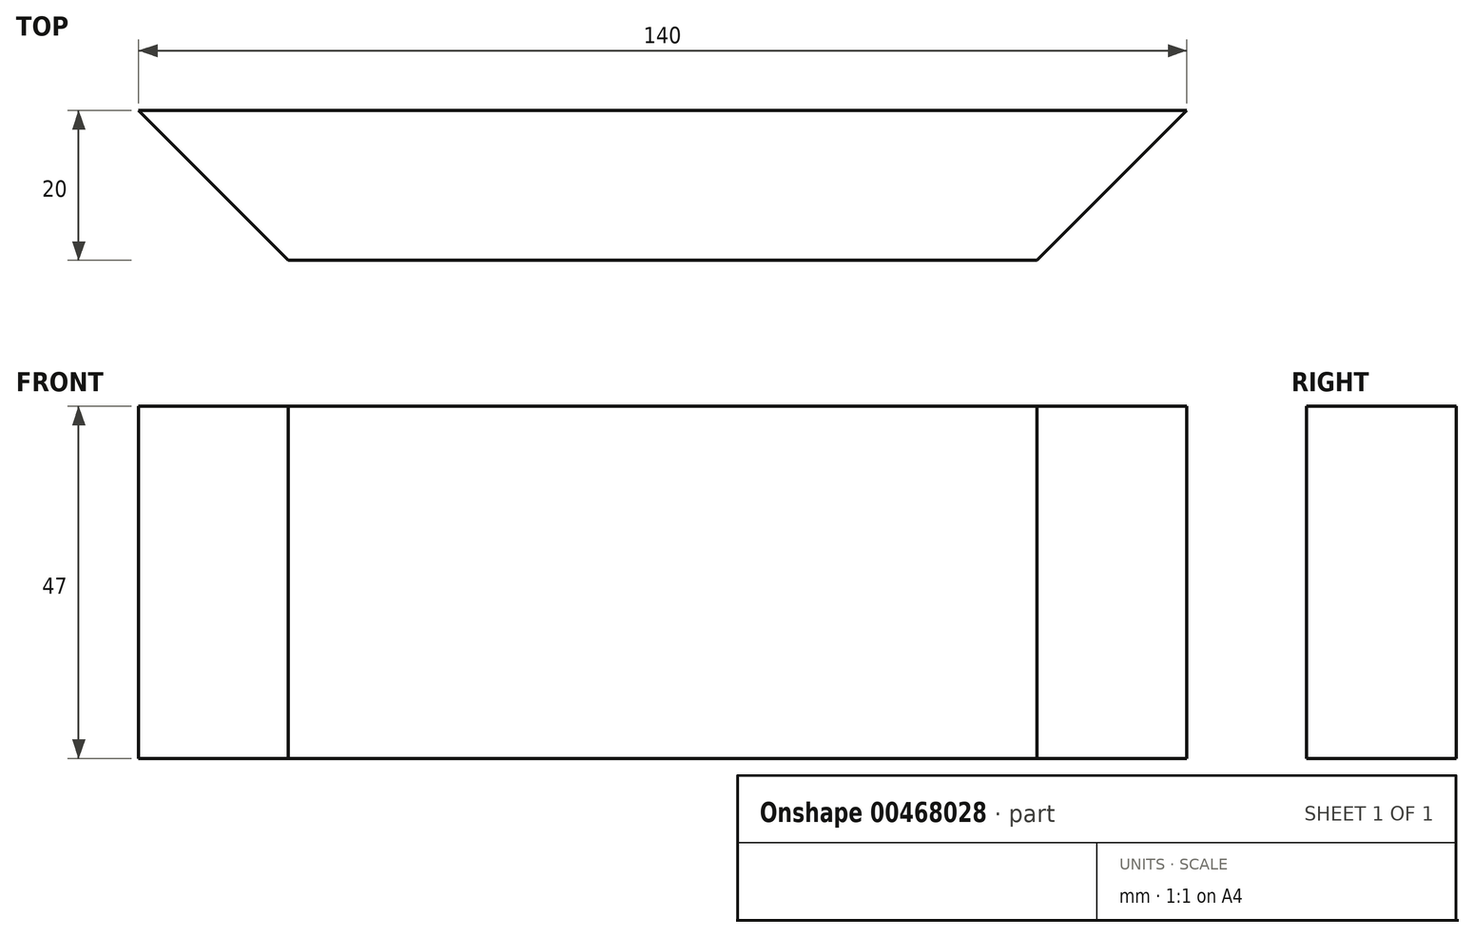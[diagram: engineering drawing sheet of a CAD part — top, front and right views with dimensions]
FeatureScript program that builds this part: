
annotation { "Feature Type Name" : "Feature", "Feature Type Description" : "" }
export const myFeature = defineFeature(function(context is Context, id is Id, definition is map)
    precondition{}
    {
        {
            var Q0;
            Q0=qCreatedBy(makeId("Top.planeOp"),FACE);
            var sketch = newSketch(context, id + "F0", { "sketchPlane" : qUnion([Q0])});
            skLineSegment(sketch, "E0", {"start": v(0, 0) * mm, "end": v(140, 0) * mm});
            skLineSegment(sketch, "E1", {"start": v(140, 0) * mm, "end": v(120, -20) * mm});
            skLineSegment(sketch, "E2", {"start": v(120, -20) * mm, "end": v(20, -20) * mm});
            skLineSegment(sketch, "E3", {"start": v(20, -20) * mm, "end": v(0, 0) * mm});
            skSolve(sketch);
        }
        {
            var Q0;
            Q0=makeQuery(id+"F0.imprint","IMPRINT",FACE,{"disambiguationData":[TD([[makeQuery(id+"F0.imprint","IMPRINT",EDGE,{"derivedFrom":sQuery(id+"F0.wireOp",EDGE,"E0")}),-1.0]])]});
            extrude(context, id + "F1", {"entities" : qUnion([Q0]), "depth" : 47 * mm, "offsetDistance" : 25 * mm});
        }
    });
